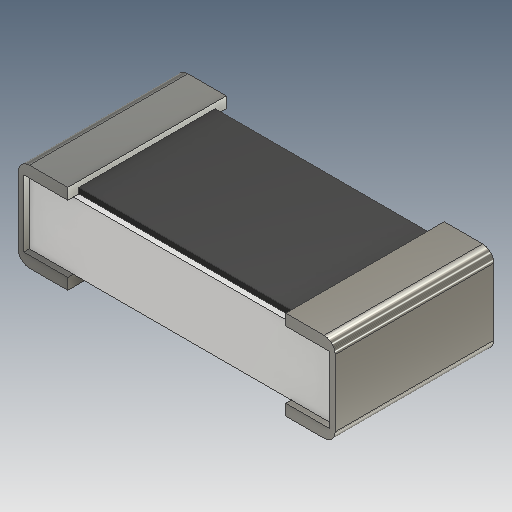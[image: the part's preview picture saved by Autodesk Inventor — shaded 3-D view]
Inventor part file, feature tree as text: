
AUTODESK INVENTOR PART (.ipt)
format: ipt  version: 2018 (Build 220112000, 112)  size: 233,984 bytes
history: native  units: mm
features: other x13, extrude x6, sketch x6, projected_geometry x5, mirror x2, fillet x1
ambient origin geometry x8: Origin, YZ Plane, XZ Plane, XY Plane, X Axis, Y Axis, Z Axis, Center Point
bodies: Solid1 (feature_tree)
feature tree (33):
  other  "Table"
  other  "chipResistor-0075"
  other  "chipResistor-0100"
  other  "chipResistor-0201"
  other  "chipResistor-0402"
  other  "chipResistor-0603"
  other  "chipResistor-0805"
  other  "chipResistor-1206"
  other  "chipResistor-1210"
  other  "chipResistor-1218"
  other  "chipResistor-2010"
  other  "chipResistor-2512W"
  other  "chipResistor-2512WW"
  extrude  "Extrusion1"  Depth=1.6mm
  extrude  "Extrusion2"  TaperAngle=0.0deg  [1 undecoded]
  extrude  "Extrusion7"  Depth=0.25mm
  extrude  "Extrusion8"  TaperAngle=0.0deg  [1 undecoded]
  mirror  "Mirror1"
  extrude  "Extrusion9"  Depth=0.25mm
  extrude  "Extrusion10"  TaperAngle=0.0deg  [1 undecoded]
  mirror  "Mirror2"
  fillet  "Fillet1"  Radius=0.028125mm
  sketch  "Sketch1"  dims[d0=0.8mm d1=1.6mm]
  sketch  "Sketch2"  dims[d2=0.45mm d3=0.0mm]
  projected_geometry  "Projected Loop1"
  sketch  "Sketch3"  dims[d4=0.25mm d5=0.25mm]
  projected_geometry  "Projected Loop2"
  sketch  "Sketch4"  dims[d6=0.05625mm d7=0.0mm]
  projected_geometry  "Projected Loop3"
  sketch  "Sketch7"  dims[d21=0.05625mm d22=0.25mm]
  projected_geometry  "Projected Loop6"
  sketch  "Sketch8"  dims[d23=0.05625mm d24=0.0mm d25=0.028125mm d26=0.028125mm d27=0.028125mm d28=0.0mm d29=0.028125mm d30=0.0mm d31=0.028125mm d32=0.0mm]
  projected_geometry  "Projected Loop7"
note: 3 required parameter values undecoded (feature->parameter linkage not recoverable at this tier; creation-order binding heuristic only, values carry confidence <= 0.55)
